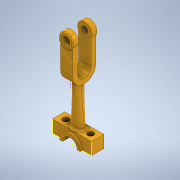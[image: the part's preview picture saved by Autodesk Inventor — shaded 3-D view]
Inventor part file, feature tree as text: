
AUTODESK INVENTOR PART (.ipt)
format: ipt  version: 2020 (Build 240168000, 168)  size: 368,128 bytes
history: native  units: mm
features: sketch x17, extrude x12, fillet x4, projected_geometry x4, plane x2, loft x1, thread x1
ambient origin geometry x8: Origin, YZ Plane, XZ Plane, XY Plane, X Axis, Y Axis, Z Axis, Center Point
bodies: Solid1 (feature_tree)
feature tree (41):
  extrude  "Extrusion1"  Depth=6.0mm
  extrude  "Extrusion2"  Depth=10.0mm
  extrude  "Extrusion3"  Depth=7.0mm
  extrude  "Extrusion4"  Depth=3.0mm
  sketch  "Sketch5"  dims[d13=3.0mm d14=12.0mm]
  plane  "Work Plane1"
  loft  "Loft1"
  sketch  "Sketch8"  dims[d20=25.0mm d21=2.945mm]
  sketch  "Sketch9"  dims[d22=2.0mm d23=2.5mm]
  plane  "Work Plane2"
  extrude  "Extrusion5"  Depth=3.0mm
  extrude  "Extrusion6"  Depth=6.0mm TaperAngle=0.0deg
  extrude  "Extrusion7"  Depth=2.945mm
  extrude  "Extrusion8"  Depth=2.5mm
  sketch  "Sketch14"  dims[d45=2.0mm d46=0.0mm]
  extrude  "Extrusion9"  TaperAngle=0.0deg  [1 undecoded]
  fillet  "Fillet1"  [1 undecoded]
  fillet  "Fillet2"  Radius=45.0mm
  fillet  "Fillet3"  Radius=9.5mm
  extrude  "Extrusion10"  Depth=11.0mm
  extrude  "Extrusion11"  Depth=6.0mm TaperAngle=0.0deg
  extrude  "Extrusion12"  Depth=3.0mm TaperAngle=0.0deg
  thread  "Thread1"  [1 undecoded]
  fillet  "Fillet4"  Radius=2.0mm
  sketch  "Sketch1"  dims[d0=19.0mm d1=6.0mm]
  sketch  "Sketch2"  dims[d2=6.0mm d3=0.0mm d4=10.0mm]
  projected_geometry  "Projected Loop1"
  sketch  "Sketch3"  dims[d5=1.0mm d6=7.0mm d7=0.0mm d8=0.0mm d9=7.0mm]
  sketch  "Sketch4"  dims[d10=8.0mm d11=0.0mm d12=3.0mm]
  sketch  "Sketch6"  dims[d15=3.5mm d16=3.0mm]
  sketch  "Sketch7"  dims[d17=3.0mm d18=6.0mm d19=0.0mm]
  sketch  "Sketch10"  dims[d24=1.5mm d25=0.0mm d26=90.0deg d27=0.0mm d28=90.0deg d29=45.0mm d30=9.5mm]
  sketch  "Sketch11"  dims[d31=9.5mm d32=11.0mm]
  sketch  "Sketch12"  dims[d33=6.0mm d34=6.0mm d35=0.0mm]
  projected_geometry  "Projected Loop2"
  projected_geometry  "Projected Loop3"
  sketch  "Sketch13"  dims[d36=7.0mm d37=3.0mm d38=9.0mm d39=0.0mm d40=0.0mm d41=6.0mm d42=0.0mm d43=2.0mm d44=0.0mm]
  projected_geometry  "Projected Loop4"
  sketch  "Sketch15"  dims[d47=1.0mm]
  sketch  "Sketch16"  dims[d48=0.5mm]
  sketch  "Sketch17"  dims[d49=0.5mm d50=6.5mm d51=0.0mm d52=20.0mm d53=0.0mm d54=3.0mm d55=2.75mm d56=0.0mm d57=4.0mm d58=2.75mm d59=0.0mm d60=10.0mm d61=0.0mm d62=1.0mm]
note: 3 required parameter values undecoded (feature->parameter linkage not recoverable at this tier; creation-order binding heuristic only, values carry confidence <= 0.55)
